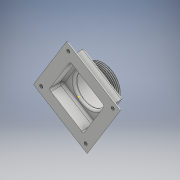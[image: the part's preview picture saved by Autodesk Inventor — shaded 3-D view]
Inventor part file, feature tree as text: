
AUTODESK INVENTOR PART (.ipt)
format: ipt  version: 2018 (Build 220112000, 112)  size: 1,983,488 bytes
history: native  units: mm
features: sketch x18, revolve x7, thread x6, plane x5, helix x5, fillet x5, extrude x3, hole x1
ambient origin geometry x8: Origin, YZ Plane, XZ Plane, XY Plane, X Axis, Y Axis, Z Axis, Center Point
bodies: Solid1 (feature_tree), Solid2 (feature_tree), Solid3 (feature_tree), Solid4 (feature_tree), Solid5 (feature_tree), Solid6 (feature_tree), Solid7 (feature_tree)
feature tree (50):
  revolve  "Revolution1"  [1 undecoded]
  thread  "Thread1"  [1 undecoded]
  plane  "Work Plane1"
  sketch  "Sketch5"  dims[d3=90.0deg d4=10.0mm d5=0.0mm]
  extrude  "Extrusion1"  Depth=10.0mm TaperAngle=0.0deg
  plane  "Work Plane2"
  extrude  "Extrusion2"  Depth=42.5mm
  plane  "Work Plane3"
  sketch  "Sketch8"  dims[d31=42.5mm d32=5.0mm d33=0.0mm d34=0.0mm]
  thread  "Thread2"  [1 undecoded]
  revolve  "Revolution4"  [1 undecoded]
  revolve  "Revolution5"  [1 undecoded]
  helix  "Coil2"  [1 undecoded]
  plane  "Work Plane5"
  extrude  "Extrusion4"  Depth=5.0mm
  plane  "Work Plane6"
  hole  "Hole3"  [1 undecoded]
  thread  "Thread3"  [1 undecoded]
  thread  "Thread4"  [1 undecoded]
  thread  "Thread5"  [1 undecoded]
  thread  "Thread6"  [1 undecoded]
  revolve  "Revolution6"  [1 undecoded]
  helix  "Coil3"  [1 undecoded]
  revolve  "Revolution7"  [1 undecoded]
  helix  "Coil4"  [1 undecoded]
  revolve  "Revolution8"  [1 undecoded]
  helix  "Coil5"  [1 undecoded]
  fillet  "Fillet1"  Radius=21.0mm
  fillet  "Fillet2"  Radius=96.0mm
  fillet  "Fillet3"  Radius=96.0mm
  fillet  "Fillet4"  Radius=96.0mm
  fillet  "Fillet5"  Radius=4.0mm
  revolve  "Revolution9"  [1 undecoded]
  helix  "Coil6"  [1 undecoded]
  sketch  "Sketch1"  dims[d0=5.0mm d1=20.0mm d2=27.75mm]
  sketch  "Sketch6"  dims[d13=9.599311mm d27=42.5mm d28=85.0mm]
  sketch  "Sketch7"  dims[d29=85.0mm d30=85.0mm]
  sketch  "Sketch10"  dims[d35=5.0mm d36=85.0mm]
  sketch  "Sketch11"  dims[d37=80.0mm d38=5.0mm d39=5.0mm d40=80.0mm d41=80.0mm d42=5.0mm]
  sketch  "Sketch12"  dims[d43=20.0mm d44=0.0mm d45=0.0mm d55=10.0mm d56=0.0mm]
  sketch  "Sketch18"  dims[d57=9.599311mm d58=0.480249mm d59=0.480249mm d62=3.0mm d64=9.599311mm]
  sketch  "Sketch19"  dims[d66=0.0mm d67=0.0mm]
  sketch  "Sketch20"  dims[d68=3.003mm d69=26.0mm d70=10.0mm d71=0.0mm d72=0.0mm d73=0.0mm d74=0.0mm d75=0.0mm d98=19.25mm d99=21.0mm d100=96.0mm d101=96.0mm d102=96.0mm d103=4.0mm d104=0.0mm]
  sketch  "Sketch21"  dims[d105=4.0mm d106=10.0mm d107=10.0mm]
  sketch  "Sketch22"  dims[d108=10.0mm]
  sketch  "Sketch23"  dims[d109=6.0mm d110=6.0mm d111=4.0mm d112=2.0mm d113=90.0deg d114=0.5mm]
  sketch  "Sketch24"  dims[d115=20.594885mm]
  sketch  "Sketch25"  dims[d116=10.0mm d117=0.0mm]
  sketch  "Sketch26"  dims[d118=10.0mm d119=0.0mm]
  sketch  "Sketch27"  dims[d120=10.0mm d121=0.0mm d122=10.0mm d123=0.0mm d126=9.599311mm d127=0.160083mm d128=0.160083mm d131=1.0mm d133=9.599311mm d135=0.0mm d136=1.001mm d137=6.0mm d138=10.0mm d139=0.0mm d140=0.0mm d141=0.0mm d142=0.0mm d143=0.0mm d144=9.599311mm d145=0.160083mm d146=0.160083mm d149=1.0mm d151=9.599311mm d153=0.0mm d154=1.001mm d155=6.0mm d156=10.0mm d157=0.0mm d158=0.0mm d159=0.0mm d160=0.0mm d161=0.0mm d162=9.599311mm d163=0.160083mm d164=0.160083mm d167=1.0mm d169=9.599311mm d171=0.0mm d172=1.001mm d173=6.0mm d174=10.0mm d175=0.0mm d176=0.0mm d177=0.0mm d178=0.0mm d179=0.0mm d180=3.0mm d181=4.0mm d182=4.0mm d183=4.0mm d184=4.0mm d185=9.599311mm d186=0.160083mm d187=0.160083mm d190=1.0mm d192=9.599311mm d194=0.0mm d195=1.001mm d196=6.0mm d197=10.0mm d198=0.0mm d199=0.0mm d200=0.0mm d201=0.0mm d202=0.0mm]
note: 19 required parameter values undecoded (feature->parameter linkage not recoverable at this tier; creation-order binding heuristic only, values carry confidence <= 0.55)